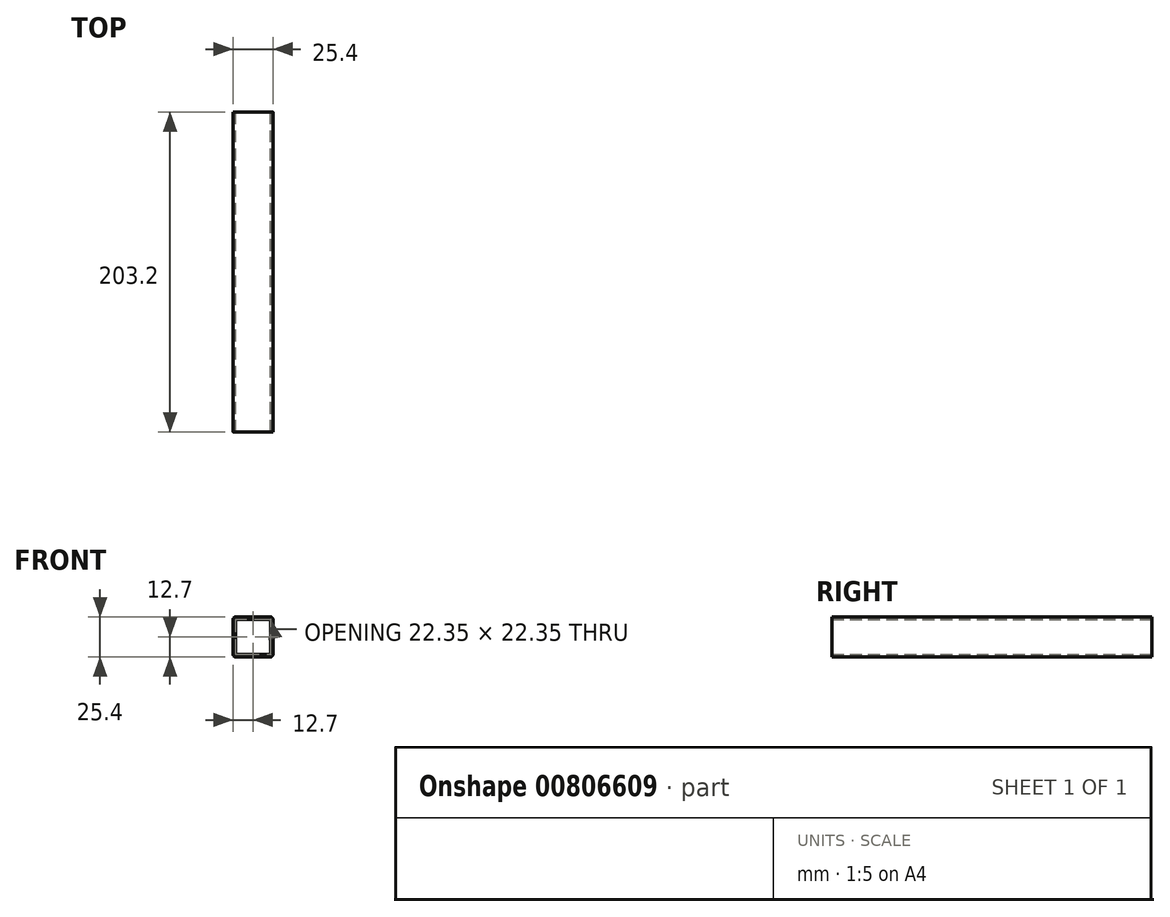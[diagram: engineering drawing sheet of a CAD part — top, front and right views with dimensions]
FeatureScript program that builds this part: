
annotation { "Feature Type Name" : "Feature", "Feature Type Description" : "" }
export const myFeature = defineFeature(function(context is Context, id is Id, definition is map)
    precondition{}
    {
        {
            var Q0;
            Q0=qCreatedBy(makeId("Front.planeOp"),FACE);
            var sketch = newSketch(context, id + "F0", { "sketchPlane" : qUnion([Q0])});
            skLineSegment(sketch, "E0.bottom", {"start": v(1.65, 0) * mm, "end": v(23.75, 0) * mm});
            skLineSegment(sketch, "E0.top", {"start": v(1.65, 25.4) * mm, "end": v(23.75, 25.4) * mm});
            skLineSegment(sketch, "E0.left", {"start": v(0, 1.65) * mm, "end": v(0, 23.75) * mm});
            skLineSegment(sketch, "E0.right", {"start": v(25.4, 1.65) * mm, "end": v(25.4, 23.75) * mm});
            skPoint(sketch, "E1.visualSharp", {"position": v(25.4, 25.4) * mm});
            skArc(sketch, "E1.filletArc", {"start": v(25.4, 23.75) * mm, "mid": v(24.92, 24.92) * mm, "end": v(23.75, 25.4) * mm});
            skPoint(sketch, "E2.visualSharp", {"position": v(0, 25.4) * mm});
            skArc(sketch, "E2.filletArc", {"start": v(1.65, 25.4) * mm, "mid": v(0.48, 24.92) * mm, "end": v(0, 23.75) * mm});
            skPoint(sketch, "E3.visualSharp", {"position": v(0, 0) * mm});
            skArc(sketch, "E3.filletArc", {"start": v(0, 1.65) * mm, "mid": v(0.48, 0.48) * mm, "end": v(1.65, 0) * mm});
            skPoint(sketch, "E4.visualSharp", {"position": v(25.4, 0) * mm});
            skArc(sketch, "E4.filletArc", {"start": v(23.75, 0) * mm, "mid": v(24.92, 0.48) * mm, "end": v(25.4, 1.65) * mm});
            skArc(sketch, "E5.0", {"start": v(1.65, 23.88) * mm, "mid": v(1.56, 23.84) * mm, "end": v(1.52, 23.75) * mm});
            skLineSegment(sketch, "E5.1", {"start": v(1.52, 1.65) * mm, "end": v(1.52, 23.75) * mm});
            skLineSegment(sketch, "E5.2", {"start": v(1.65, 23.88) * mm, "end": v(23.75, 23.88) * mm});
            skArc(sketch, "E5.3", {"start": v(1.52, 1.65) * mm, "mid": v(1.56, 1.56) * mm, "end": v(1.65, 1.52) * mm});
            skArc(sketch, "E5.4", {"start": v(23.88, 23.75) * mm, "mid": v(23.84, 23.84) * mm, "end": v(23.75, 23.88) * mm});
            skLineSegment(sketch, "E5.5", {"start": v(23.88, 1.65) * mm, "end": v(23.88, 23.75) * mm});
            skArc(sketch, "E5.6", {"start": v(23.75, 1.52) * mm, "mid": v(23.84, 1.56) * mm, "end": v(23.88, 1.65) * mm});
            skLineSegment(sketch, "E5.7", {"start": v(1.65, 1.52) * mm, "end": v(23.75, 1.52) * mm});
            skSolve(sketch);
        }
        {
            var Q0;
            Q0 = qSketchRegion(id + "F0", true);
            extrude(context, id + "F1", {"entities" : qUnion([Q0]), "depth" : 203.2 * mm, "offsetDistance" : 25.4 * mm});
        }
    });
